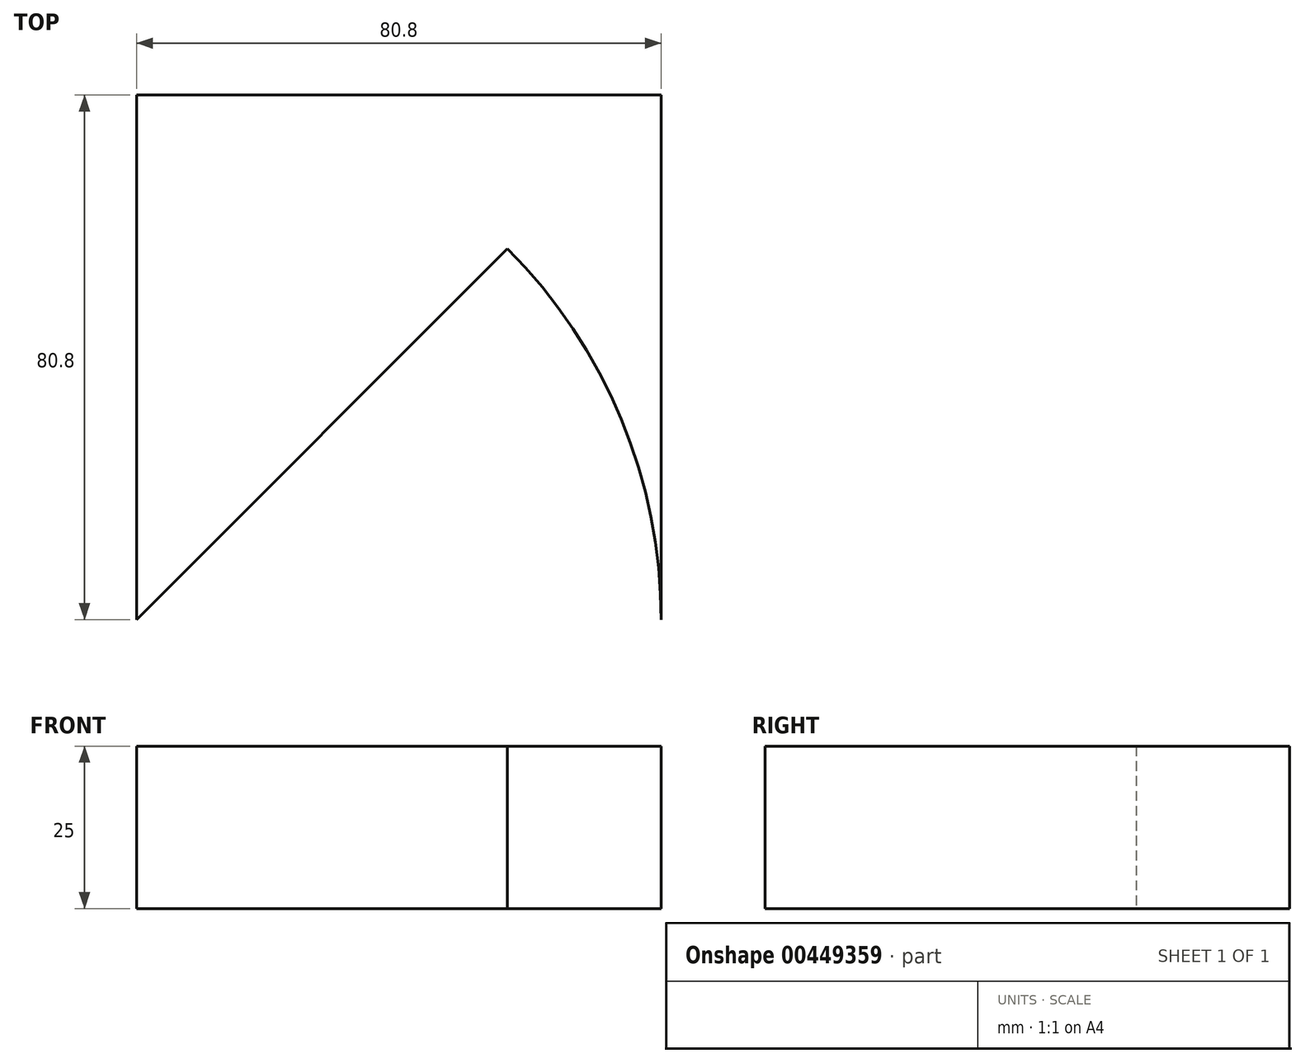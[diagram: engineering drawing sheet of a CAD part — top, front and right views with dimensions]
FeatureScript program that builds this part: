
annotation { "Feature Type Name" : "Feature", "Feature Type Description" : "" }
export const myFeature = defineFeature(function(context is Context, id is Id, definition is map)
    precondition{}
    {
        {
            var Q0;
            Q0=qCreatedBy(makeId("Top.planeOp"),FACE);
            var sketch = newSketch(context, id + "F0", { "sketchPlane" : qUnion([Q0])});
            skLineSegment(sketch, "E0.bottom", {"start": v(-40.4, 40.4) * mm, "end": v(40.4, 40.4) * mm});
            skLineSegment(sketch, "E0.top", {"start": v(-40.4, -40.4) * mm, "end": v(40.4, -40.4) * mm});
            skLineSegment(sketch, "E0.left", {"start": v(-40.4, 40.4) * mm, "end": v(-40.4, -40.4) * mm});
            skLineSegment(sketch, "E0.right", {"start": v(40.4, 40.4) * mm, "end": v(40.4, -40.4) * mm});
            skPoint(sketch, "E0.middle", {"position": v(0, 0) * mm});
            skSolve(sketch);
        }
        {
            var Q0;
            Q0=makeQuery(id+"F0.imprint","IMPRINT",FACE,{"disambiguationData":[TD([[makeQuery(id+"F0.imprint","IMPRINT",EDGE,{"derivedFrom":sQuery(id+"F0.wireOp",EDGE,"E0.bottom")}),-1.0]])]});
            extrude(context, id + "F1", {"entities" : qUnion([Q0]), "depth" : 25 * mm});
        }
        {
            var Q0;
            Q0=makeQuery(id+"F1.opExtrude","SWEPT_FACE",FACE,{"disambiguationData":[OSD([sQuery(id+"F0.wireOp",EDGE,"E0.top")])]});
            var Q1;
            Q1=makeQuery(id+"F1.opExtrude","SWEPT_EDGE",EDGE,{"disambiguationData":[OSD([sQuery(id+"F0.wireOp",EDGE,"E0.top"),sQuery(id+"F0.wireOp",EDGE,"E0.left")])]});
            revolve(context, id + "F2", {"operationType" : NewBodyOperationType.REMOVE, "entities" : qUnion([Q0]), "axis" : qUnion([Q1]), "revolveType" : RevolveType.ONE_DIRECTION, "oppositeDirection" : true, "angle" : 45 * degree});
        }
    });
